# Revit family: RoofAccessHatch_Kattsafe_Hinged
name_source: partatom
category: Specialty Equipment
units: mm (PartAtom-declared; Revit-internal decimal feet)

## family parameters
Always vertical = No
Cut with Voids When Loaded = Yes
Enable Cutting in Views = No
Maintain Annotation Orientation = No
OmniClass Number = 23.17.11.27.17
Part Type = Normal
Room Calculation Point = No
Round Connector Dimension = Use Diameter
Shared = No
Work Plane-Based = Yes

## types (2) — shared parameters
Assembly Code = E1090100
Description = Access hatches allow for safe, secure access onto a roof from inside of a building, reducing the risk of a fall by minimising time spent at the edge of a roof. Kattsafe roof access hatches are designed with large openings for easy personnel access, even with tools and equipment, as well as safe and easy operation.
ElementType = Access Hatch
Export Type to IFC As = IfcBuildingElementProxy
FlashingUpstandHeight = 145 mm  [stored 0.475722 ft]
HatchOpeningDepth = 800 mm  [stored 2.62467 ft]
HatchOpeningWidth = 1000 mm  [stored 3.28084 ft]
IfcExportAs = IfcBuildingElementProxy
IfcExportType = USERDEFINED
Manufacturer = Kattsafe®
ManufacturerOverallHeight = 195 mm  [stored 0.639764 ft]
ManufacturerURLProductSpecific = https://kattsafe.com.au
Material = Steel_Zincalume_Kattsafe
ModifiedIssue = 20240430 $
Type IFC Predefined Type = USERDEFINED
URL = https://kattsafe.com.au
Uniclass2015Code = Pr_30_59_36_74
Uniclass2015Title = Roof hatches
Uniclass2015Version = Products v1.23
zero-valued in all types: Default Elevation

## per-type parameters (varying)
| type | CorrugatedDeckFlashing | FlashingDepthEnds | FlashingDepthSides | ManufacturerOverallDepth | ManufacturerOverallWidth | ManufacturerSpecCode | Model | TrayDeckFlashing | Type Comments |
| Tray Deck Flashing (LD494T) | No | 182 mm  [stored 0.597113 ft] | 149 mm  [stored 0.488845 ft] | 1098 mm  [stored 3.60236 ft] | 1364 mm | LD494T | LD494T | Yes | Roof Access Hatch - Hinged - Tray Deck Flashing |
| Corrugated Deck Flashing (LD494C) | Yes | 180 mm  [stored 0.590551 ft] | 181 mm  [stored 0.593832 ft] | 1162 mm  [stored 3.81234 ft] | 1360 mm  [stored 4.46194 ft] | LD494C | LD494C | No | Roof Access Hatch - Hinged - Corrugated Flashing |

note: [stored X ft] marks values corroborated as IEEE doubles in the binary element streams (Revit-internal decimal feet)

## geometry (parser evidence)
native form markers: Sweep x9
no freeform markers — native parametric forms only
